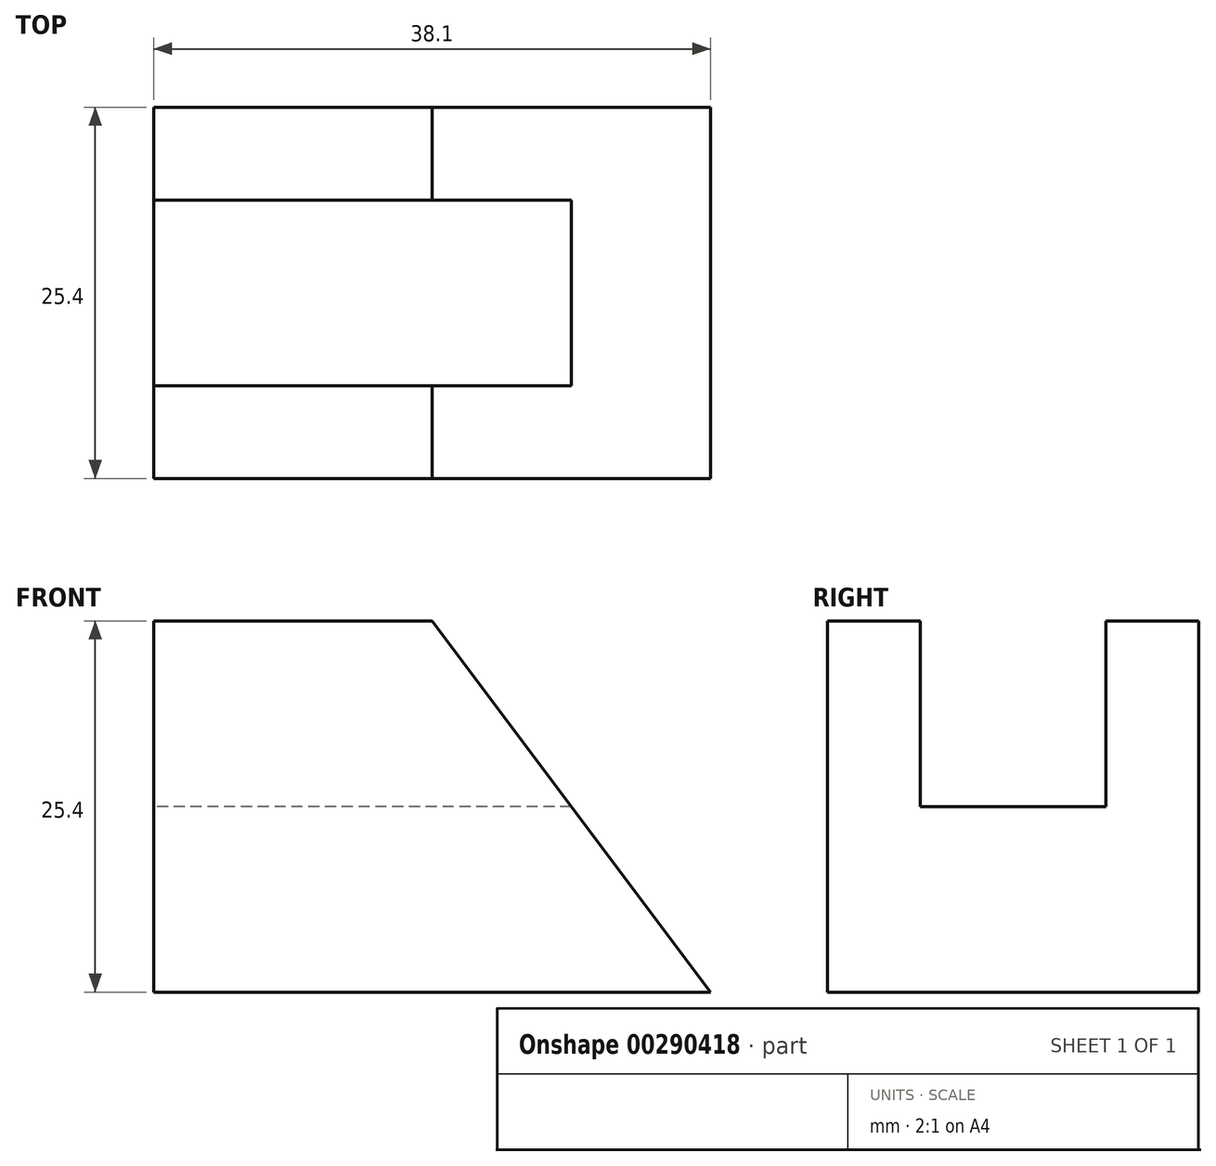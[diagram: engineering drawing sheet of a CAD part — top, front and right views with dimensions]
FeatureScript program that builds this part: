
annotation { "Feature Type Name" : "Feature", "Feature Type Description" : "" }
export const myFeature = defineFeature(function(context is Context, id is Id, definition is map)
    precondition{}
    {
        {
            var Q0;
            Q0=qCreatedBy(makeId("Front.planeOp"),FACE);
            var sketch = newSketch(context, id + "F0", { "sketchPlane" : qUnion([Q0])});
            skLineSegment(sketch, "E0", {"start": v(-14.67, 0) * mm, "end": v(-14.67, 25.4) * mm});
            skLineSegment(sketch, "E1", {"start": v(-14.67, 25.4) * mm, "end": v(4.38, 25.4) * mm});
            skLineSegment(sketch, "E2", {"start": v(4.38, 25.4) * mm, "end": v(23.43, 0) * mm});
            skLineSegment(sketch, "E3", {"start": v(23.43, 0) * mm, "end": v(-14.67, 0) * mm});
            skSolve(sketch);
        }
        {
            var Q0;
            Q0 = qSketchRegion(id + "F0", true);
            extrude(context, id + "F1", {"entities" : qUnion([Q0]), "depth" : 25.4 * mm});
        }
        {
            var Q0;
            Q0=makeQuery(id+"F1.opExtrude","SWEPT_FACE",FACE,{"disambiguationData":[OSD([sQuery(id+"F0.wireOp",EDGE,"E0")])]});
            var sketch = newSketch(context, id + "F2", { "sketchPlane" : qUnion([Q0])});
            skLineSegment(sketch, "E4", {"start": v(6.35, 25.4) * mm, "end": v(6.35, 12.7) * mm});
            skLineSegment(sketch, "E5", {"start": v(6.35, 12.7) * mm, "end": v(19.05, 12.7) * mm});
            skLineSegment(sketch, "E6", {"start": v(19.05, 12.7) * mm, "end": v(19.05, 25.4) * mm});
            skLineSegment(sketch, "E7", {"start": v(19.05, 25.4) * mm, "end": v(6.35, 25.4) * mm});
            skSolve(sketch);
        }
        {
            var Q0;
            Q0 = qSketchRegion(id + "F2", true);
            extrude(context, id + "F3", {"entities" : qUnion([Q0]), "operationType" : NewBodyOperationType.REMOVE, "oppositeDirection" : true, "depth" : 76.2 * mm});
        }
    });
